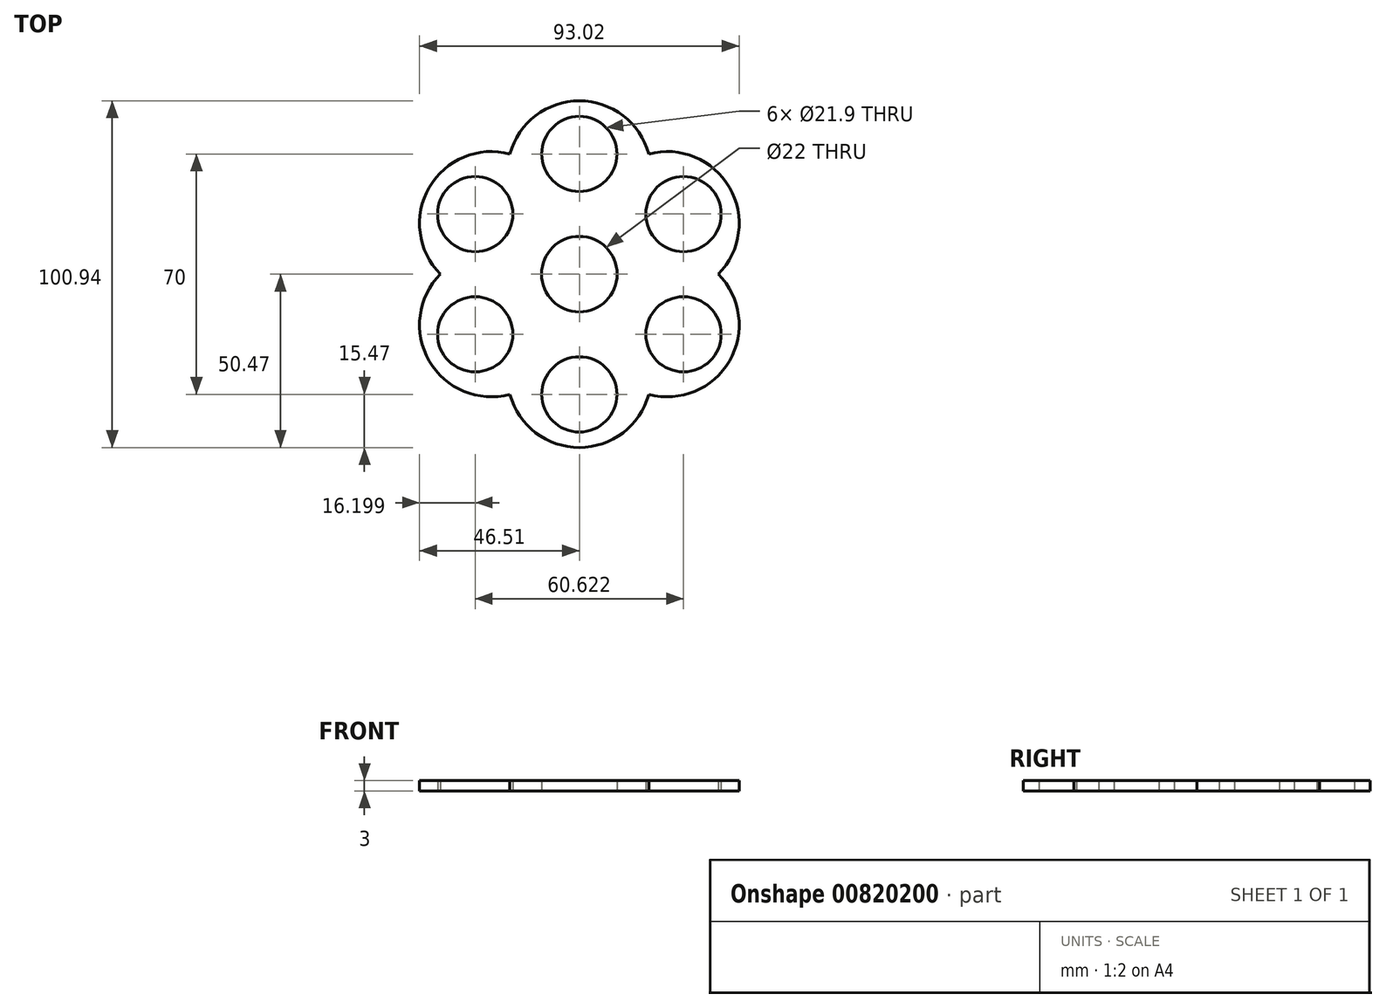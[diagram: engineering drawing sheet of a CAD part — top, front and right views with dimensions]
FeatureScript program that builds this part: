
annotation { "Feature Type Name" : "Feature", "Feature Type Description" : "" }
export const myFeature = defineFeature(function(context is Context, id is Id, definition is map)
    precondition{}
    {
        {
            var Q0;
            Q0=qCreatedBy(makeId("Top.planeOp"),FACE);
            var sketch = newSketch(context, id + "F0", { "sketchPlane" : qUnion([Q0])});
            skArc(sketch, "E0", {"start": v(5.75, 9.38) * mm, "mid": v(0, 11) * mm, "end": v(-5.75, 9.38) * mm});
            skCircle(sketch, "E1", {"center": v(0, 35) * mm, "radius": 10.95 * mm});
            skArc(sketch, "E2", {"start": v(20.21, 35.01) * mm, "mid": v(0, 50.47) * mm, "end": v(-20.21, 35.01) * mm});
            skArc(sketch, "E3.trimOffspring", {"start": v(-5.75, 9.38) * mm, "mid": v(-5.55, 9.32) * mm, "end": v(-5.35, 9.27) * mm});
            skArc(sketch, "E4.trimOffspring", {"start": v(5.35, 9.27) * mm, "mid": v(5.55, 9.32) * mm, "end": v(5.75, 9.38) * mm});
            skArc(sketch, "E5.1.0", {"start": v(-20.21, 35.01) * mm, "mid": v(-43.7, 25.23) * mm, "end": v(-40.43, 0) * mm});
            skCircle(sketch, "E5.1.1", {"center": v(-30.31, 17.5) * mm, "radius": 10.95 * mm});
            skArc(sketch, "E5.1.2", {"start": v(-5.25, 9.67) * mm, "mid": v(-9.53, 5.5) * mm, "end": v(-11, -0.3) * mm});
            skArc(sketch, "E5.2.0", {"start": v(-40.43, 0) * mm, "mid": v(-43.7, -25.23) * mm, "end": v(-20.21, -35.01) * mm});
            skCircle(sketch, "E5.2.1", {"center": v(-30.31, -17.5) * mm, "radius": 10.95 * mm});
            skArc(sketch, "E5.2.2", {"start": v(-11, 0.3) * mm, "mid": v(-9.53, -5.5) * mm, "end": v(-5.25, -9.67) * mm});
            skArc(sketch, "E5.3.0", {"start": v(-20.21, -35.01) * mm, "mid": v(0, -50.47) * mm, "end": v(20.21, -35.01) * mm});
            skCircle(sketch, "E5.3.1", {"center": v(0, -35) * mm, "radius": 10.95 * mm});
            skArc(sketch, "E5.3.2", {"start": v(-5.75, -9.38) * mm, "mid": v(0, -11) * mm, "end": v(5.75, -9.38) * mm});
            skArc(sketch, "E5.4.0", {"start": v(20.21, -35.01) * mm, "mid": v(43.7, -25.23) * mm, "end": v(40.43, 0) * mm});
            skCircle(sketch, "E5.4.1", {"center": v(30.31, -17.5) * mm, "radius": 10.95 * mm});
            skArc(sketch, "E5.4.2", {"start": v(5.25, -9.67) * mm, "mid": v(9.53, -5.5) * mm, "end": v(11, 0.3) * mm});
            skArc(sketch, "E5.5.0", {"start": v(40.43, 0) * mm, "mid": v(43.7, 25.23) * mm, "end": v(20.21, 35.01) * mm});
            skCircle(sketch, "E5.5.1", {"center": v(30.31, 17.5) * mm, "radius": 10.95 * mm});
            skArc(sketch, "E5.5.2", {"start": v(11, -0.3) * mm, "mid": v(9.53, 5.5) * mm, "end": v(5.25, 9.67) * mm});
            skSolve(sketch);
        }
        {
            var Q0;
            Q0 = qSketchRegion(id + "F0", true);
            extrude(context, id + "F1", {"entities" : qUnion([Q0]), "depth" : 3 * mm, "offsetDistance" : 25 * mm});
        }
    });
